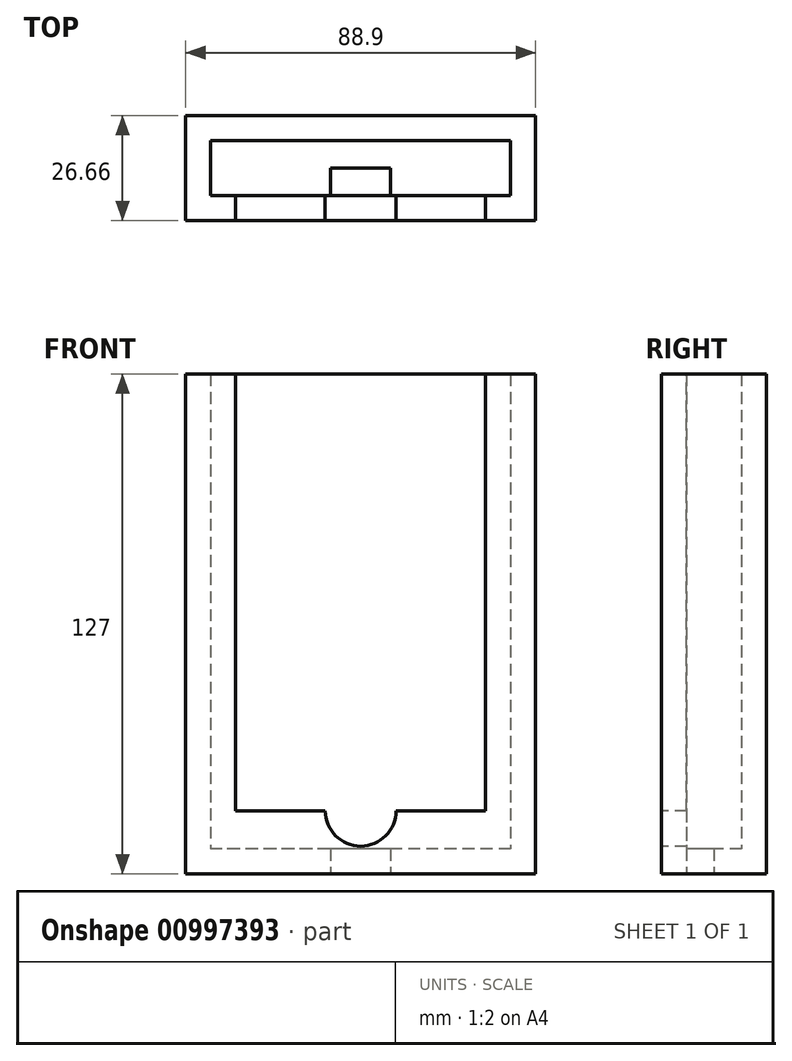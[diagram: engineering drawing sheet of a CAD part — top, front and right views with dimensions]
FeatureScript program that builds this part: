
annotation { "Feature Type Name" : "Feature", "Feature Type Description" : "" }
export const myFeature = defineFeature(function(context is Context, id is Id, definition is map)
    precondition{}
    {
        {
            var Q0;
            Q0=qCreatedBy(makeId("Top.planeOp"),FACE);
            var sketch = newSketch(context, id + "F0", { "sketchPlane" : qUnion([Q0])});
            skLineSegment(sketch, "E0.bottom", {"start": v(38.1, 6.98) * mm, "end": v(-38.1, 6.98) * mm});
            skLineSegment(sketch, "E0.top", {"start": v(38.1, -6.98) * mm, "end": v(-38.1, -6.99) * mm});
            skLineSegment(sketch, "E0.left", {"start": v(38.1, 6.98) * mm, "end": v(38.1, -6.99) * mm});
            skLineSegment(sketch, "E0.right", {"start": v(-38.1, 6.98) * mm, "end": v(-38.1, -6.99) * mm});
            skPoint(sketch, "E0.middle", {"position": v(0, 0) * mm});
            skLineSegment(sketch, "E1.0", {"start": v(44.45, 13.33) * mm, "end": v(44.45, -13.33) * mm});
            skLineSegment(sketch, "E1.1", {"start": v(44.45, 13.33) * mm, "end": v(-44.45, 13.33) * mm});
            skLineSegment(sketch, "E1.2", {"start": v(-44.45, 13.33) * mm, "end": v(-44.45, -13.34) * mm});
            skLineSegment(sketch, "E1.3", {"start": v(44.45, -13.33) * mm, "end": v(-44.45, -13.34) * mm});
            skPoint(sketch, "E2.right.start.orphan", {"position": v(-6.35, 3.81) * mm});
            skPoint(sketch, "E2.top.end.orphan", {"position": v(-6.35, -3.81) * mm});
            skPoint(sketch, "E2.left.end.orphan", {"position": v(6.35, -3.81) * mm});
            skPoint(sketch, "E2.left.start.orphan", {"position": v(6.35, 3.81) * mm});
            skLineSegment(sketch, "E3.bottom", {"start": v(7.62, 0) * mm, "end": v(-7.62, 0) * mm});
            skLineSegment(sketch, "E3.top", {"start": v(7.62, -6.99) * mm, "end": v(-7.62, -6.99) * mm});
            skLineSegment(sketch, "E3.left", {"start": v(7.62, 0) * mm, "end": v(7.62, -6.99) * mm});
            skLineSegment(sketch, "E3.right", {"start": v(-7.62, 0) * mm, "end": v(-7.62, -6.99) * mm});
            skPoint(sketch, "E3.middle", {"position": v(0, -3.5) * mm});
            skSolve(sketch);
        }
        {
            var Q0;
            Q0=makeQuery(id+"F0.imprint","IMPRINT",FACE,{"disambiguationData":[TD([[makeQuery(id+"F0.imprint","IMPRINT",EDGE,{"derivedFrom":sQuery(id+"F0.wireOp",EDGE,"E0.bottom")}),1.0]])]});
            extrude(context, id + "F1", {"entities" : qUnion([Q0]), "depth" : 6.35 * mm, "offsetDistance" : 25.4 * mm});
        }
        {
            var Q0;
            Q0=makeQuery(id+"F0.imprint","IMPRINT",FACE,{"disambiguationData":[TD([[makeQuery(id+"F0.imprint","IMPRINT",EDGE,{"derivedFrom":sQuery(id+"F0.wireOp",EDGE,"E0.bottom")}),-1.0]])]});
            extrude(context, id + "F2", {"entities" : qUnion([Q0]), "operationType" : NewBodyOperationType.ADD, "depth" : 127 * mm, "offsetDistance" : 25.4 * mm});
        }
        {
            var Q0;
            Q0=makeQuery(id+"F2.opExtrude","SWEPT_FACE",FACE,{"disambiguationData":[OSD([sQuery(id+"F0.wireOp",EDGE,"E1.3")])]});
            var sketch = newSketch(context, id + "F3", { "sketchPlane" : qUnion([Q0])});
            skLineSegment(sketch, "E4.bottom", {"start": v(-31.75, 127) * mm, "end": v(31.75, 127) * mm});
            skLineSegment(sketch, "E4.top", {"start": v(-31.75, 16.04) * mm, "end": v(31.75, 16.04) * mm});
            skLineSegment(sketch, "E4.left", {"start": v(-31.75, 127) * mm, "end": v(-31.75, 16.04) * mm});
            skLineSegment(sketch, "E4.right", {"start": v(31.75, 127) * mm, "end": v(31.75, 16.04) * mm});
            skCircle(sketch, "E5", {"center": v(0, 16.04) * mm, "radius": 9 * mm});
            skPoint(sketch, "E5.centerSnap0", {"position": v(0, 16.04) * mm});
            skSolve(sketch);
        }
        {
            var Q0;
            Q0 = qSketchRegion(id + "F3", true);
            extrude(context, id + "F4", {"entities" : qUnion([Q0]), "operationType" : NewBodyOperationType.REMOVE, "endBound" : BoundingType.UP_TO_NEXT, "oppositeDirection" : true, "depth" : 25.4 * mm, "offsetDistance" : 25.4 * mm});
        }
    });
